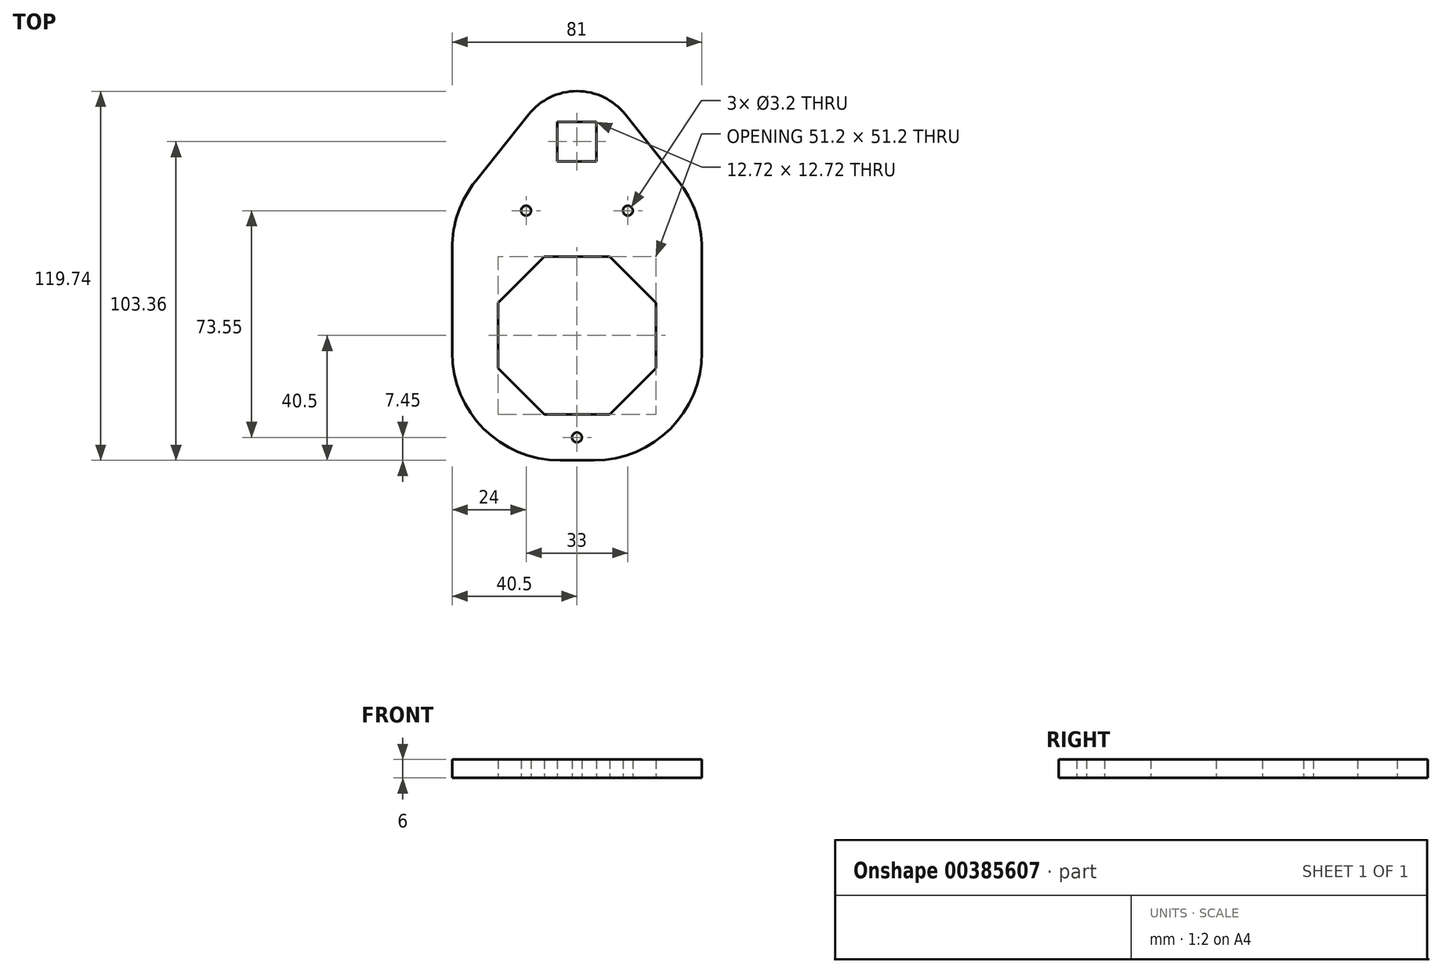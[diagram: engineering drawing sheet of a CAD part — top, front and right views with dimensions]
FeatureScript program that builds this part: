
annotation { "Feature Type Name" : "Feature", "Feature Type Description" : "" }
export const myFeature = defineFeature(function(context is Context, id is Id, definition is map)
    precondition{}
    {
        {
            var Q0;
            Q0=qCreatedBy(makeId("Top.planeOp"),FACE);
            var sketch = newSketch(context, id + "F0", { "sketchPlane" : qUnion([Q0])});
            skLineSegment(sketch, "E0.bottom", {"start": v(0, 0) * mm, "end": v(51.2, 0) * mm, "construction": true});
            skLineSegment(sketch, "E0.top", {"start": v(0, 51.2) * mm, "end": v(51.2, 51.2) * mm, "construction": true});
            skLineSegment(sketch, "E0.left", {"start": v(0, 0) * mm, "end": v(0, 51.2) * mm, "construction": true});
            skLineSegment(sketch, "E0.right", {"start": v(51.2, 0) * mm, "end": v(51.2, 51.2) * mm, "construction": true});
            skLineSegment(sketch, "E1", {"start": v(0, 36.2) * mm, "end": v(15, 51.2) * mm});
            skLineSegment(sketch, "E2", {"start": v(36.2, 0) * mm, "end": v(51.2, 15) * mm});
            skLineSegment(sketch, "E3", {"start": v(36.2, 51.2) * mm, "end": v(51.2, 36.2) * mm});
            skLineSegment(sketch, "E4", {"start": v(0, 15) * mm, "end": v(15, 0) * mm});
            skCircle(sketch, "E5", {"center": v(25.6, 25.6) * mm, "radius": 25.6 * mm, "construction": true});
            skPoint(sketch, "E5.centerSnap0", {"position": v(0, 25.6) * mm});
            skPoint(sketch, "E6", {"position": v(25.6, 51.2) * mm});
            skLineSegment(sketch, "E7", {"start": v(-14.9, 66.1) * mm, "end": v(-14.9, -14.9) * mm});
            skLineSegment(sketch, "E8", {"start": v(-14.9, -14.9) * mm, "end": v(66.1, -14.9) * mm});
            skLineSegment(sketch, "E9", {"start": v(66.1, -14.9) * mm, "end": v(66.1, 66.1) * mm});
            skLineSegment(sketch, "E10", {"start": v(66.1, 66.1) * mm, "end": v(-14.9, 66.1) * mm, "construction": true});
            skLineSegment(sketch, "E11", {"start": v(-14.9, 25.6) * mm, "end": v(66.1, 25.6) * mm, "construction": true});
            skLineSegment(sketch, "E12", {"start": v(25.6, -14.9) * mm, "end": v(25.6, 66.1) * mm, "construction": true});
            skLineSegment(sketch, "E13", {"start": v(-14.9, 66.1) * mm, "end": v(25.6, 116.94) * mm});
            skLineSegment(sketch, "E14", {"start": v(66.1, 66.1) * mm, "end": v(25.6, 116.94) * mm});
            skLineSegment(sketch, "E15", {"start": v(0, 36.2) * mm, "end": v(0, 15) * mm});
            skLineSegment(sketch, "E16", {"start": v(15, 51.2) * mm, "end": v(36.2, 51.2) * mm});
            skLineSegment(sketch, "E17", {"start": v(51.2, 36.2) * mm, "end": v(51.2, 15) * mm});
            skLineSegment(sketch, "E18", {"start": v(15, 0) * mm, "end": v(36.2, 0) * mm});
            skLineSegment(sketch, "E19.bottom", {"start": v(31.96, 94.82) * mm, "end": v(19.24, 94.82) * mm});
            skLineSegment(sketch, "E19.top", {"start": v(31.96, 82.1) * mm, "end": v(19.24, 82.1) * mm});
            skLineSegment(sketch, "E19.left", {"start": v(31.96, 94.82) * mm, "end": v(31.96, 82.1) * mm});
            skLineSegment(sketch, "E19.right", {"start": v(19.24, 94.82) * mm, "end": v(19.24, 82.1) * mm});
            skLineSegment(sketch, "E20", {"start": v(25.6, 66.1) * mm, "end": v(25.6, 116.94) * mm, "construction": true});
            skPoint(sketch, "E21", {"position": v(25.6, 94.82) * mm});
            skCircle(sketch, "E22", {"center": v(9.1, 66.1) * mm, "radius": 1.6 * mm});
            skCircle(sketch, "E23", {"center": v(42.1, 66.1) * mm, "radius": 1.6 * mm});
            skPoint(sketch, "E24", {"position": v(25.6, 0) * mm});
            skPoint(sketch, "E25", {"position": v(25.6, -7.45) * mm});
            skCircle(sketch, "E26", {"center": v(25.6, -7.45) * mm, "radius": 1.6 * mm});
            skSolve(sketch);
        }
        {
            var Q0;
            Q0 = qSketchRegion(id + "F0", true);
            extrude(context, id + "F1", {"entities" : qUnion([Q0]), "depth" : 6 * mm});
        }
        {
            var Q0;
            Q0=makeQuery(id+"F1.opExtrude","SWEPT_EDGE",EDGE,{"disambiguationData":[OSD([sQuery(id+"F0.wireOp",EDGE,"E8"),sQuery(id+"F0.wireOp",EDGE,"E9")])]});
            var Q1;
            Q1=makeQuery(id+"F1.opExtrude","SWEPT_EDGE",EDGE,{"disambiguationData":[OSD([sQuery(id+"F0.wireOp",EDGE,"E7"),sQuery(id+"F0.wireOp",EDGE,"E8")])]});
            var Q2;
            Q2=makeQuery(id+"F1.opExtrude","SWEPT_EDGE",EDGE,{"disambiguationData":[OSD([sQuery(id+"F0.wireOp",EDGE,"E7"),sQuery(id+"F0.wireOp",EDGE,"E10"),sQuery(id+"F0.wireOp",EDGE,"E13")])]});
            var Q3;
            Q3=makeQuery(id+"F1.opExtrude","SWEPT_EDGE",EDGE,{"disambiguationData":[OSD([sQuery(id+"F0.wireOp",EDGE,"E9"),sQuery(id+"F0.wireOp",EDGE,"E10"),sQuery(id+"F0.wireOp",EDGE,"E14")])]});
            fillet(context, id + "F2", {"entities" : qUnion([Q0, Q1, Q2, Q3]), "radius" : 35 * mm, "tangentPropagation" : true, "allowEdgeOverflow" : false});
        }
        {
            var Q0;
            Q0=makeQuery(id+"F1.opExtrude","SWEPT_EDGE",EDGE,{"disambiguationData":[OSD([sQuery(id+"F0.wireOp",EDGE,"E13"),sQuery(id+"F0.wireOp",EDGE,"E14")])]});
            fillet(context, id + "F3", {"entities" : qUnion([Q0]), "radius" : 20 * mm, "tangentPropagation" : true, "allowEdgeOverflow" : false});
        }
    });
